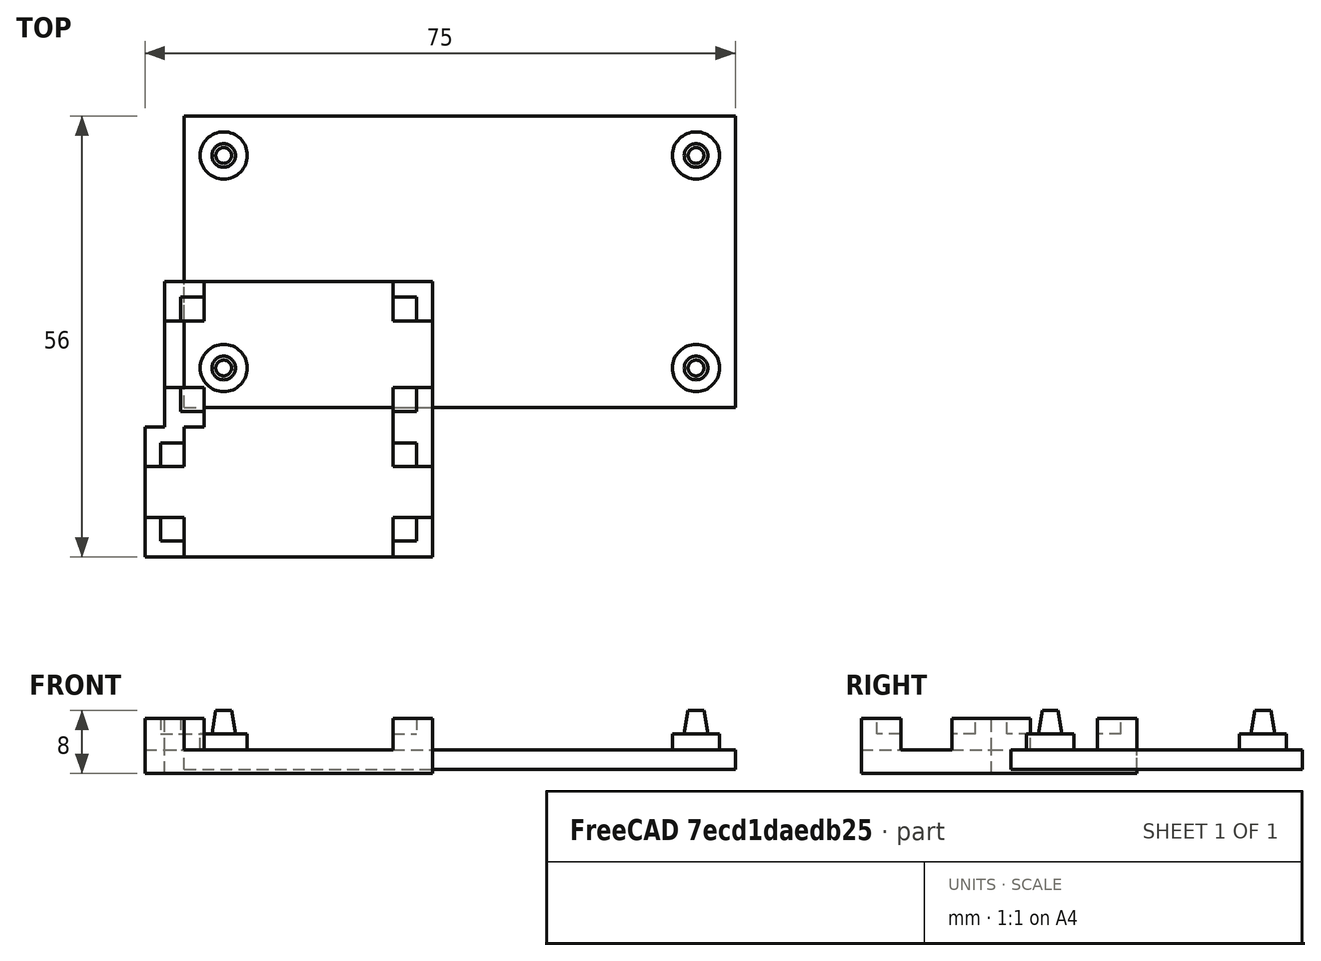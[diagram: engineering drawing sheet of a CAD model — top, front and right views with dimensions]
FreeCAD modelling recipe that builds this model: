
FCSTD DOCUMENT  (FreeCAD 0.17R13541 (Git))
Label: board_holders
License: All rights reserved
LicenseURL: http://en.wikipedia.org/wiki/All_rights_reserved
objects: PartDesign::FeatureBase×9, Part::Box×7, Part::MultiFuse×5, Part::Cut×2, Part::Cone×1, Part::Cylinder×1
note: 25 computed .brp shape members not serialized (recipe doc carries the construction recipe); baked Part::Feature solids carry a one-line shape summary decoded from their .brp

FEATURE [Part::Box] Box  label="Cube"
  AttacherType = Attacher::AttachEngine3D
  Height = 2.5
  Length = 70
  Placement = pos=(0,0,-2.5) rot=(0,0,1;0rad)
  Width = 37
FEATURE [Part::Cone] Cone
  Angle = 360
  AttacherType = Attacher::AttachEngine3D
  Height = 3
  Placement = pos=(5,5,2) rot=(0,0,1;0rad)
  Radius1 = 1.5
  Radius2 = 1
FEATURE [Part::Cylinder] Cylinder
  Angle = 360
  AttacherType = Attacher::AttachEngine3D
  Height = 2
  Placement = pos=(5,5,0) rot=(0,0,1;0rad)
  Radius = 3
FEATURE [Part::MultiFuse] Fusion
  Shapes = -> [Cone,Cylinder]
FEATURE [PartDesign::FeatureBase] Clone
  BaseFeature = -> Fusion
  Placement = pos=(60,0,0) rot=(0,0,1;0rad)
FEATURE [PartDesign::FeatureBase] Clone001
  BaseFeature = -> Fusion
  Placement = pos=(60,27,0) rot=(0,0,1;0rad)
FEATURE [PartDesign::FeatureBase] Clone002
  BaseFeature = -> Fusion
  Placement = pos=(0,27,0) rot=(0,0,1;0rad)
FEATURE [Part::MultiFuse] Fusion001  label="mcu_holder"
  Shapes = -> [Box,Clone002,Fusion,Clone001,Clone]
FEATURE [Part::Box] Box001  label="Cube001"
  AttacherType = Attacher::AttachEngine3D
  Height = 3
  Length = 34
  Placement = pos=(-2.5,-2.5,-3) rot=(0,0,1;0rad)
  Width = 18.5
FEATURE [Part::Box] Box002  label="Cube002"
  AttacherType = Attacher::AttachEngine3D
  Height = 10
  Length = 30
  Placement = pos=(-0.5,-0.5,2) rot=(0,0,1;0rad)
  Width = 14.5
FEATURE [Part::Box] Box003  label="Cube003"
  AttacherType = Attacher::AttachEngine3D
  Height = 4
  Length = 5
  Placement = pos=(-2.5,-2.5,0) rot=(0,0,1;0rad)
  Width = 5
FEATURE [PartDesign::FeatureBase] Clone003
  BaseFeature = -> Box003
  Placement = pos=(26.5,-2.5,0) rot=(0,0,1;0rad)
FEATURE [PartDesign::FeatureBase] Clone004
  BaseFeature = -> Box003
  Placement = pos=(26.5,11,0) rot=(0,0,1;0rad)
FEATURE [PartDesign::FeatureBase] Clone005
  BaseFeature = -> Box003
  Placement = pos=(-2.5,11,0) rot=(0,0,1;0rad)
FEATURE [Part::MultiFuse] Fusion002
  Shapes = -> [Box001,Box003,Clone003,Clone004,Clone005]
FEATURE [Part::Cut] Cut  label="preamp_holder"
  Base = -> Fusion002
  Tool = -> Box002
FEATURE [Part::Box] Box004  label="Cube004"
  AttacherType = Attacher::AttachEngine3D
  Height = 6
  Length = 32.5
  Placement = pos=(2,2,2) rot=(0,0,1;0rad)
  Width = 12.5
FEATURE [Part::Box] Box005  label="Cube005"
  AttacherType = Attacher::AttachEngine3D
  Height = 3
  Length = 36.5
  Placement = pos=(0,0,-3) rot=(0,0,1;0rad)
  Width = 16.5
FEATURE [Part::Box] Box006  label="Cube006"
  AttacherType = Attacher::AttachEngine3D
  Height = 4
  Length = 5
  Width = 5
FEATURE [PartDesign::FeatureBase] Clone006
  BaseFeature = -> Box006
  Placement = pos=(31.5,0,0) rot=(0,0,1;0rad)
FEATURE [PartDesign::FeatureBase] Clone007
  BaseFeature = -> Box006
  Placement = pos=(31.5,11.5,0) rot=(0,0,1;0rad)
FEATURE [PartDesign::FeatureBase] Clone008
  BaseFeature = -> Box006
  Placement = pos=(0,11.5,0) rot=(0,0,1;0rad)
FEATURE [Part::MultiFuse] Fusion003
  Shapes = -> [Box005,Box006,Clone006,Clone007,Clone008]
FEATURE [Part::Cut] Cut001  label="ref_holder"
  Base = -> Fusion003
  Placement = pos=(-5,-19,0) rot=(0,0,1;0rad)
  Tool = -> Box004
FEATURE [Part::MultiFuse] Fusion004  label="combined_holder"
  Shapes = -> [Cut,Cut001]
